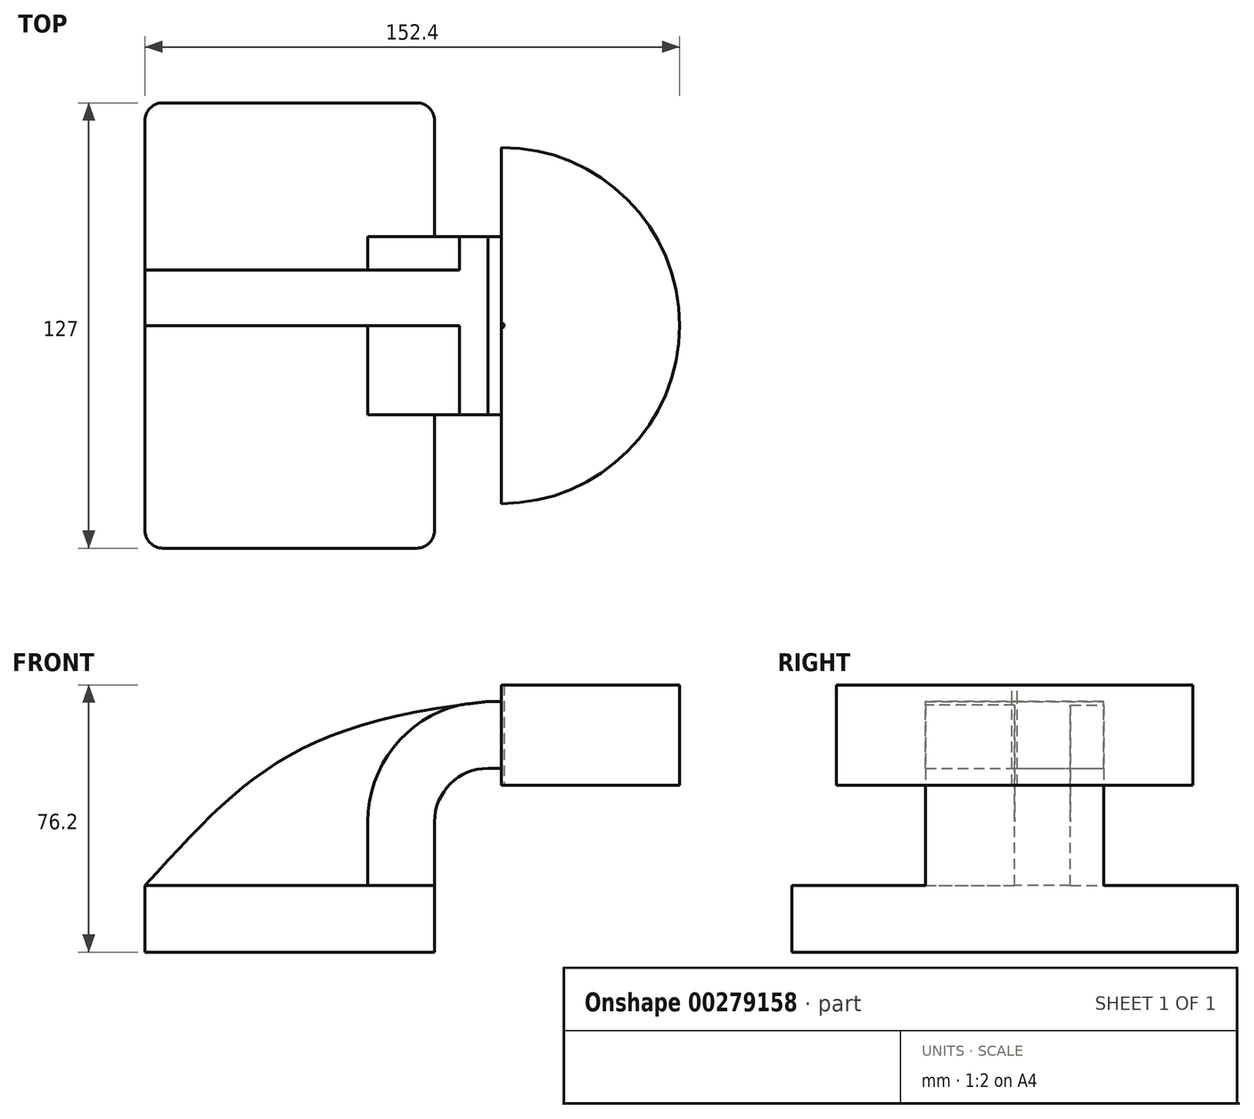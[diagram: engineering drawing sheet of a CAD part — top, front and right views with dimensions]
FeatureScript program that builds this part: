
annotation { "Feature Type Name" : "Feature", "Feature Type Description" : "" }
export const myFeature = defineFeature(function(context is Context, id is Id, definition is map)
    precondition{}
    {
        {
            var Q0;
            Q0=qCreatedBy(makeId("Front.planeOp"),FACE);
            var sketch = newSketch(context, id + "F0", { "sketchPlane" : qUnion([Q0])});
            skLineSegment(sketch, "E0.bottom", {"start": v(-41.28, 9.52) * mm, "end": v(41.27, 9.53) * mm});
            skLineSegment(sketch, "E0.top", {"start": v(-41.28, -9.53) * mm, "end": v(41.28, -9.53) * mm});
            skLineSegment(sketch, "E0.left", {"start": v(-41.28, 9.52) * mm, "end": v(-41.28, -9.53) * mm});
            skLineSegment(sketch, "E0.right", {"start": v(41.27, 9.53) * mm, "end": v(41.28, -9.52) * mm});
            skPoint(sketch, "E0.middle", {"position": v(0, 0) * mm});
            skLineSegment(sketch, "E1.bottom", {"start": v(111.13, 38.1) * mm, "end": v(60.32, 38.1) * mm});
            skLineSegment(sketch, "E1.top", {"start": v(111.12, 66.68) * mm, "end": v(60.32, 66.67) * mm});
            skLineSegment(sketch, "E1.left", {"start": v(111.12, 38.1) * mm, "end": v(111.12, 66.68) * mm});
            skLineSegment(sketch, "E1.right", {"start": v(60.32, 38.1) * mm, "end": v(60.32, 66.67) * mm});
            skPoint(sketch, "E1.middle", {"position": v(85.72, 52.39) * mm});
            skLineSegment(sketch, "E2", {"start": v(41.27, 9.53) * mm, "end": v(41.27, 27.64) * mm});
            skArc(sketch, "E3", {"start": v(41.27, 27.64) * mm, "mid": v(45.74, 38.41) * mm, "end": v(56.51, 42.88) * mm});
            skLineSegment(sketch, "E4", {"start": v(56.51, 42.88) * mm, "end": v(72.64, 42.88) * mm});
            skLineSegment(sketch, "E5.0", {"start": v(61.1, 38.1) * mm, "end": v(61.1, 69.85) * mm});
            skLineSegment(sketch, "E6.0", {"start": v(56.51, 61.93) * mm, "end": v(75.06, 61.93) * mm});
            skArc(sketch, "E6.1", {"start": v(22.22, 27.64) * mm, "mid": v(32.27, 51.88) * mm, "end": v(56.51, 61.93) * mm});
            skLineSegment(sketch, "E6.2", {"start": v(22.22, 9.53) * mm, "end": v(22.22, 27.64) * mm});
            skLineSegment(sketch, "E7", {"start": v(75.06, 61.93) * mm, "end": v(75.06, 38.1) * mm});
            skFitSpline(sketch, "E8", {"points": [v(-41.28, 9.52) * mm, v(56.51, 61.93) * mm], "startDerivative": vector(82.94, 89.86) * mm, "endDerivative": vector(169.54, 18) * mm});
            skSolve(sketch);
        }
        {
            var Q0;
            Q0=makeQuery(id+"F0.imprint","IMPRINT",FACE,{"disambiguationData":[TD([[makeQuery(id+"F0.imprint","IMPRINT",EDGE,{"derivedFrom":sQuery(id+"F0.wireOp",EDGE,"E0.top")}),1.0]])]});
            extrude(context, id + "F1", {"entities" : qUnion([Q0]), "endBound" : BoundingType.SYMMETRIC, "depth" : 127 * mm});
        }
        {
            var Q0;
            {var subQ2=sQuery(id+"F0.wireOp",EDGE,"E2");Q0=makeQuery(id+"F0.imprint","IMPRINT",FACE,{"disambiguationData":[TD([[makeQuery(id+"F0.imprint","IMPRINT",EDGE,{"derivedFrom":subQ2}),1.0]])]});}
            extrude(context, id + "F2", {"entities" : qUnion([Q0]), "operationType" : NewBodyOperationType.ADD, "endBound" : BoundingType.SYMMETRIC, "depth" : 50.8 * mm});
        }
        {
            var Q0;
            {var subQ3=sQuery(id+"F0.wireOp",EDGE,"E6.2");Q0=makeQuery(id+"F0.imprint","IMPRINT",FACE,{"disambiguationData":[TD([[makeQuery(id+"F0.imprint","IMPRINT",EDGE,{"derivedFrom":subQ3}),1.0]])]});}
            extrude(context, id + "F3", {"entities" : qUnion([Q0]), "operationType" : NewBodyOperationType.ADD, "oppositeDirection" : true, "depth" : 15.88 * mm});
        }
        {
            var Q0;
            {var subQ0=sQuery(id+"F0.wireOp",EDGE,"E1.left");Q0=makeQuery(id+"F0.imprint","IMPRINT",FACE,{"disambiguationData":[TD([[makeQuery(id+"F0.imprint","IMPRINT",EDGE,{"derivedFrom":subQ0}),1.0]])]});}
            var Q1;
            {var subQ0=sQuery(id+"F0.wireOp",EDGE,"E7");Q1=makeQuery(id+"F0.imprint","IMPRINT",FACE,{"disambiguationData":[TD([[makeQuery(id+"F0.imprint","IMPRINT",EDGE,{"derivedFrom":subQ0}),-1.0]])]});}
            var Q2;
            Q2=sQuery(id+"F0.wireOp",EDGE,"E1.right");
            revolve(context, id + "F4", {"operationType" : NewBodyOperationType.ADD, "entities" : qUnion([Q0, Q1]), "axis" : qUnion([Q2]), "revolveType" : RevolveType.SYMMETRIC, "angle" : 180 * degree});
        }
        {
            var Q0;
            Q0=makeQuery(id+"F1.opExtrude","CAP_EDGE",EDGE,{"disambiguationData":[OSD([sQuery(id+"F0.wireOp",EDGE,"E0.right")])],"isStart":false});
            var Q1;
            Q1=makeQuery(id+"F1.opExtrude","CAP_EDGE",EDGE,{"disambiguationData":[OSD([sQuery(id+"F0.wireOp",EDGE,"E0.left")])],"isStart":false});
            var Q2;
            Q2=makeQuery(id+"F1.opExtrude","CAP_EDGE",EDGE,{"disambiguationData":[OSD([sQuery(id+"F0.wireOp",EDGE,"E0.left")])],"isStart":true});
            var Q3;
            Q3=makeQuery(id+"F1.opExtrude","CAP_EDGE",EDGE,{"disambiguationData":[OSD([sQuery(id+"F0.wireOp",EDGE,"E0.right")])],"isStart":true});
            fillet(context, id + "F5", {"entities" : qUnion([Q0, Q1, Q2, Q3]), "radius" : 5.08 * mm, "tangentPropagation" : true, "allowEdgeOverflow" : false});
        }
    });
